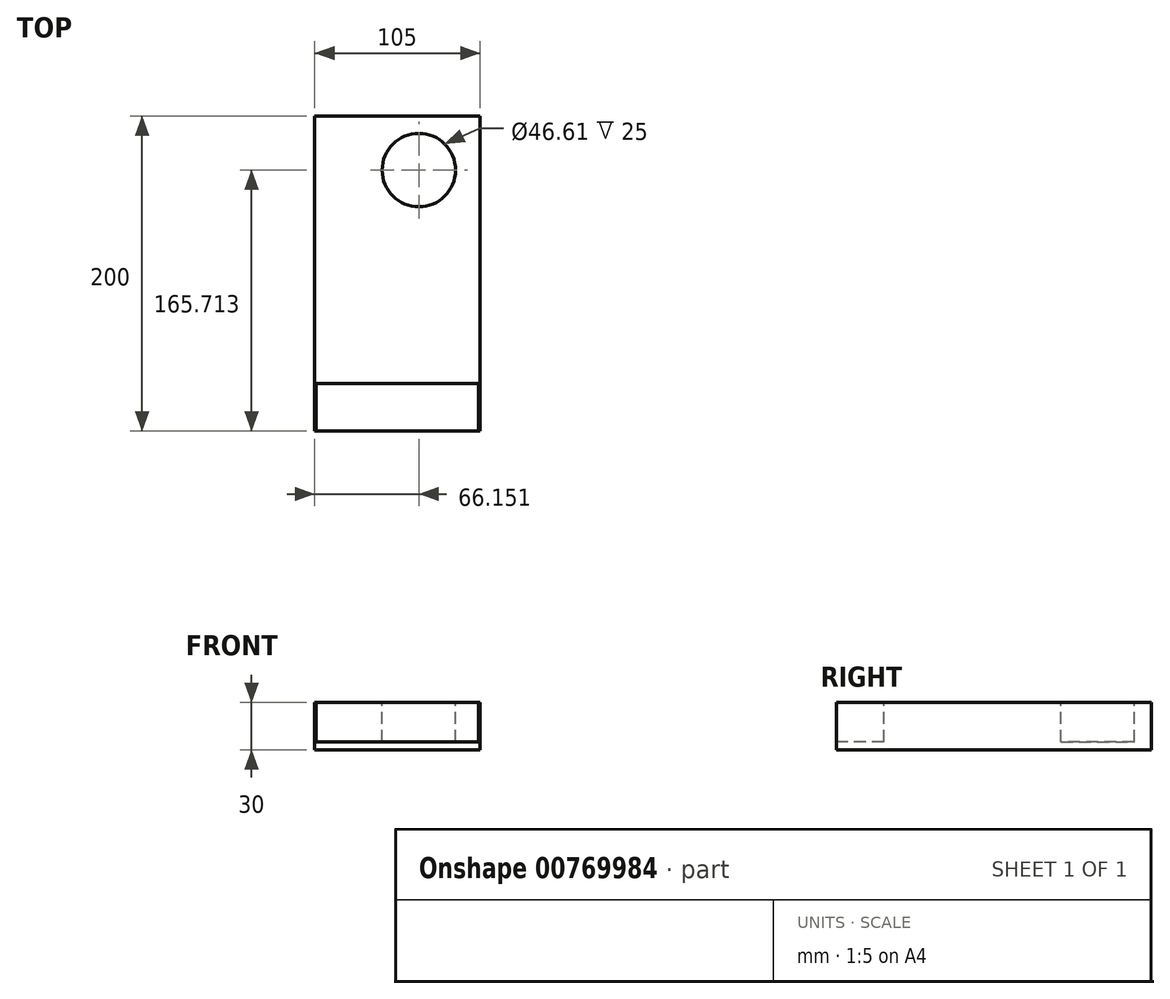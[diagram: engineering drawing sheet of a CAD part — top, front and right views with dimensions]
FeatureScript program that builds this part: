
annotation { "Feature Type Name" : "Feature", "Feature Type Description" : "" }
export const myFeature = defineFeature(function(context is Context, id is Id, definition is map)
    precondition{}
    {
        {
            var Q0;
            Q0=qCreatedBy(makeId("Top.planeOp"),FACE);
            var sketch = newSketch(context, id + "F0", { "sketchPlane" : qUnion([Q0])});
            skLineSegment(sketch, "E0.bottom", {"start": v(52.5, -100) * mm, "end": v(-52.5, -100) * mm});
            skLineSegment(sketch, "E0.top", {"start": v(52.5, 100) * mm, "end": v(-52.5, 100) * mm});
            skLineSegment(sketch, "E0.left", {"start": v(52.5, -100) * mm, "end": v(52.5, 100) * mm});
            skLineSegment(sketch, "E0.right", {"start": v(-52.5, -100) * mm, "end": v(-52.5, 100) * mm});
            skPoint(sketch, "E0.middle", {"position": v(0, 0) * mm});
            skSolve(sketch);
        }
        {
            var Q0;
            Q0=makeQuery(id+"F0.imprint","IMPRINT",FACE,{"disambiguationData":[TD([[makeQuery(id+"F0.imprint","IMPRINT",EDGE,{"derivedFrom":sQuery(id+"F0.wireOp",EDGE,"E0.bottom")}),-1.0]])]});
            extrude(context, id + "F1", {"entities" : qUnion([Q0]), "depth" : 30 * mm, "offsetDistance" : 25 * mm});
        }
        {
            var Q0;
            Q0=makeQuery(id+"F1.opExtrude","CAP_FACE",FACE,{"disambiguationData":[OSD([sQuery(id+"F0.wireOp",EDGE,"E0.bottom"),sQuery(id+"F0.wireOp",EDGE,"E0.top"),sQuery(id+"F0.wireOp",EDGE,"E0.left"),sQuery(id+"F0.wireOp",EDGE,"E0.right")])],"isStart":false});
            var sketch = newSketch(context, id + "F2", { "sketchPlane" : qUnion([Q0])});
            skLineSegment(sketch, "E1.bottom", {"start": v(51.5, -70) * mm, "end": v(-51.5, -70) * mm});
            skLineSegment(sketch, "E1.top", {"start": v(51.5, -100) * mm, "end": v(-51.5, -100) * mm});
            skLineSegment(sketch, "E1.left", {"start": v(51.5, -70) * mm, "end": v(51.5, -100) * mm});
            skLineSegment(sketch, "E1.right", {"start": v(-51.5, -70) * mm, "end": v(-51.5, -100) * mm});
            skPoint(sketch, "E1.middle", {"position": v(0, -85) * mm});
            skCircle(sketch, "E2", {"center": v(13.65, 65.71) * mm, "radius": 23.3 * mm});
            skSolve(sketch);
        }
        {
            var Q0;
            Q0=makeQuery(id+"F2.imprint","IMPRINT",FACE,{"disambiguationData":[TD([[makeQuery(id+"F2.imprint","IMPRINT",EDGE,{"derivedFrom":sQuery(id+"F2.wireOp",EDGE,"E1.bottom")}),1.0]])]});
            var Q1;
            Q1=makeQuery(id+"F2.imprint","IMPRINT",FACE,{"disambiguationData":[TD([[makeQuery(id+"F2.imprint","IMPRINT",EDGE,{"derivedFrom":sQuery(id+"F2.wireOp",EDGE,"E2")}),1.0]])]});
            extrude(context, id + "F3", {"entities" : qUnion([Q0, Q1]), "operationType" : NewBodyOperationType.REMOVE, "oppositeDirection" : true, "depth" : 25 * mm, "offsetDistance" : 25 * mm});
        }
    });
